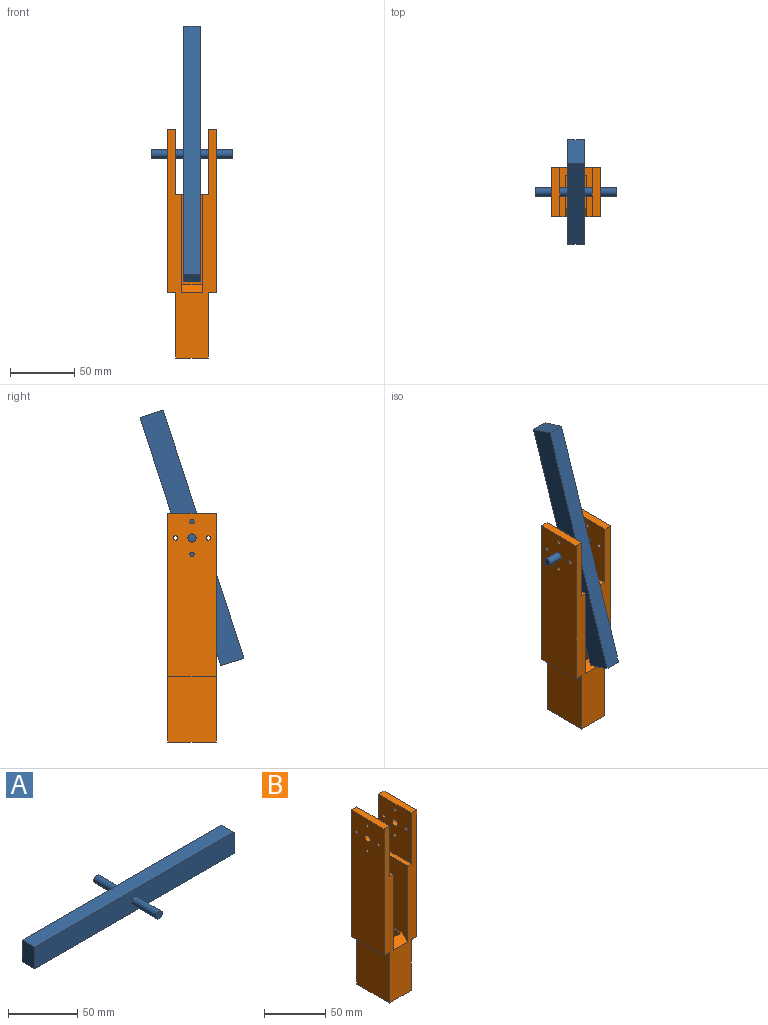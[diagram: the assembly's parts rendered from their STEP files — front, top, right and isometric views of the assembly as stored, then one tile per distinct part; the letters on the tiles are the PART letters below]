
ASSEMBLY  parts=2 mates=1
PART A: 10 faces, bbox 203.2x63.5x19.1 mm
  f0: plane 19.05x12.7mm, normal (-1,0,0), area 241.9mm2, adj f1,f3,f4,f5
  f1: plane 203.2x19.05mm, normal (0,-1,0), area 3839.3mm2, adj f0,f2,f4,f5,f8
  f2: plane 19.05x12.7mm, normal (1,0,0), area 241.9mm2, adj f1,f3,f4,f5
  f3: plane 203.2x19.05mm, normal (0,1,0), area 3839.3mm2, adj f0,f2,f4,f5,f7
  f4: plane 203.2x12.7mm, normal (0,0,1), area 2580.6mm2, adj f0,f1,f2,f3
  f5: plane 203.2x12.7mm, normal (0,0,-1), area 2580.6mm2, adj f0,f1,f2,f3
  f6: plane 6.35x6.35mm, normal (0,1,0), area 31.7mm2, adj f7
  f7: cylinder r=3.17mm len=25.4mm, axis (0,-1,0), area 506.7mm2, adj f3,f6
  f8: cylinder r=3.17mm len=25.4mm, axis (0,-1,0), area 506.7mm2, adj f1,f9
  f9: plane 6.35x6.35mm, normal (0,-1,0), area 31.7mm2, adj f8
PART B: 33 faces, bbox 38.1x38.1x177.8 mm
  f0: plane 38.1x6.35mm, normal (0,0,-1), area 241.9mm2, adj f5,f11,f17,f30
  f1: plane 25.4x1.91mm, normal (0,0,1), area 48.4mm2, adj f4,f8,f10,f21
  f2: plane 57.15x25.4mm, normal (-1,0,0), area 1451.6mm2, adj f3,f6,f10,f32
  f3: plane 57.15x12.7mm, normal (0,1,0), area 725.8mm2, adj f2,f4,f21,f32
  f4: plane 57.15x25.4mm, normal (1,0,0), area 1451.6mm2, adj f1,f3,f10,f32
  f5: plane 177.8x38.1mm, normal (0,-1,0), area 3580.6mm2, adj f0,f7,f8,f9,f12,f13,f14,f15
  f6: plane 25.4x1.91mm, normal (0,0,1), area 48.4mm2, adj f2,f9,f10,f21
  f7: plane 38.1x6.35mm, normal (0,0,-1), area 241.9mm2, adj f5,f11,f14,f31
  f8: plane 76.2x31.75mm, normal (1,0,0), area 2237.9mm2, adj f1,f5,f10,f12,f21
  f9: plane 76.2x31.75mm, normal (-1,0,0), area 2237.9mm2, adj f5,f6,f10,f12,f21
  f10: plane 127x16.51mm, normal (0,-1,0), area 1879mm2, adj f1,f2,f4,f6,f8,f9,f12,f32
  f11: plane 177.8x38.1mm, normal (0,1,0), area 4838.7mm2, adj f0,f7,f12,f13,f14,f15,f16,f17
  f12: plane 38.1x25.4mm, normal (0,0,1), area 443.5mm2, adj f5,f8,f9,f10,f11,f13,f16
  f13: plane 50.8x38.1mm, normal (1,0,0), area 1869.6mm2, adj f5,f11,f12,f15,f20,f23,f25,f27
  f14: plane 127x38.1mm, normal (-1,0,0), area 4772.8mm2, adj f5,f7,f11,f15,f20,f23,f25,f27
  f15: plane 38.1x6.35mm, normal (0,0,1), area 241.9mm2, adj f5,f11,f13,f14
  f16: plane 50.8x38.1mm, normal (-1,0,0), area 1869.6mm2, adj f5,f11,f12,f18,f19,f22,f24,f26
  f17: plane 127x38.1mm, normal (1,0,0), area 4772.8mm2, adj f0,f5,f11,f18,f19,f22,f24,f26
  f18: plane 38.1x6.35mm, normal (0,0,1), area 241.9mm2, adj f5,f11,f16,f17
  f19: cylinder r=3.17mm len=6.35mm, axis (1,0,0), area 126.7mm2, adj f16,f17
  f20: cylinder r=3.17mm len=6.35mm, axis (1,0,0), area 126.7mm2, adj f13,f14
  f21: plane 16.51x6.35mm, normal (0,-0.71,0.71), area 148.3mm2, adj f1,f3,f5,f6,f8,f9
  f22: cylinder r=1.65mm len=6.35mm, axis (1,0,0), area 65.9mm2, adj f16,f17
  f23: cylinder r=1.65mm len=6.35mm, axis (1,0,0), area 65.9mm2, adj f13,f14
  f24: cylinder r=1.65mm len=6.35mm, axis (1,0,0), area 65.9mm2, adj f16,f17
  f25: cylinder r=1.65mm len=6.35mm, axis (1,0,0), area 65.9mm2, adj f13,f14
  f26: cylinder r=1.65mm len=6.35mm, axis (1,0,0), area 65.9mm2, adj f16,f17
  f27: cylinder r=1.65mm len=6.35mm, axis (1,0,0), area 65.9mm2, adj f13,f14
  f28: cylinder r=1.65mm len=6.35mm, axis (1,0,0), area 65.9mm2, adj f16,f17
  f29: cylinder r=1.65mm len=6.35mm, axis (1,0,0), area 65.9mm2, adj f13,f14
  f30: plane 50.8x38.1mm, normal (1,0,0), area 1935.5mm2, adj f0,f5,f11,f32
  f31: plane 50.8x38.1mm, normal (-1,0,0), area 1935.5mm2, adj f5,f7,f11,f32
  f32: plane 38.1x25.4mm, normal (0,0,-1), area 645.2mm2, adj f2,f3,f4,f5,f10,f11,f30,f31
PLACE A rot(axis=(-0.63,-0.63,-0.46),130.9deg) t=(-53.3,-35.62,-7.67)mm
PLACE B t=(-46.95,4.84,-21.93)mm
MATE revolute A.f7 <-> B.f19  axis (-1,0,0) through (-66,4.84,86.02)mm
